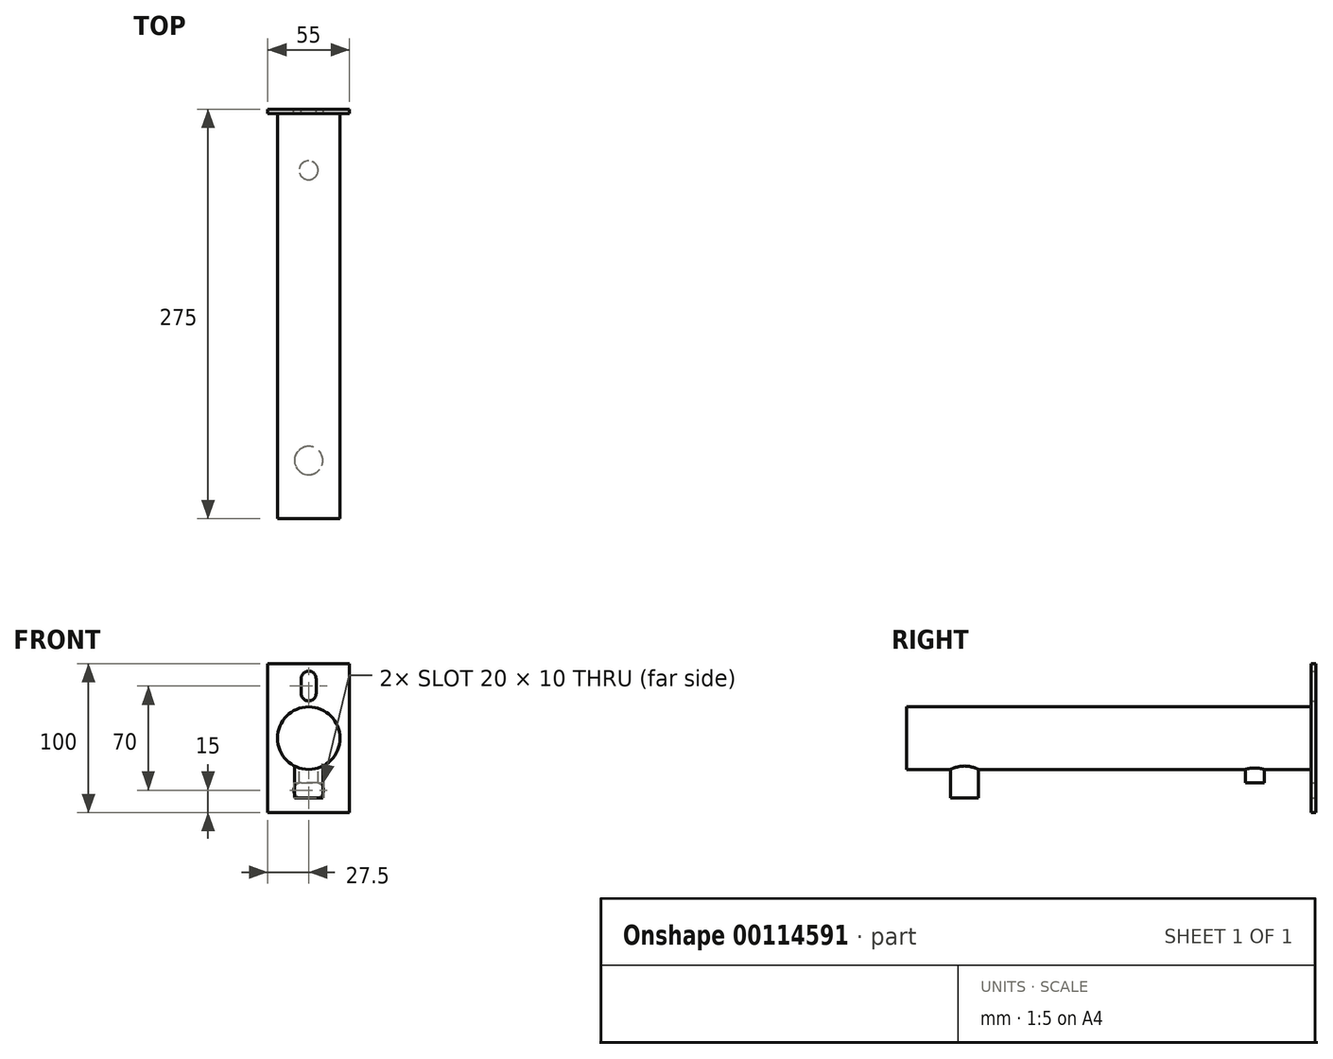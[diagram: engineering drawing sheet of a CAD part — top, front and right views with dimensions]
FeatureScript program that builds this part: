
annotation { "Feature Type Name" : "Feature", "Feature Type Description" : "" }
export const myFeature = defineFeature(function(context is Context, id is Id, definition is map)
    precondition{}
    {
        {
            var Q0;
            Q0=qCreatedBy(makeId("Front.planeOp"),FACE);
            var sketch = newSketch(context, id + "F0", { "sketchPlane" : qUnion([Q0])});
            skLineSegment(sketch, "E0.bottom", {"start": v(-27.5, -50) * mm, "end": v(27.5, -50) * mm});
            skLineSegment(sketch, "E0.top", {"start": v(-27.5, 50) * mm, "end": v(27.5, 50) * mm});
            skLineSegment(sketch, "E0.left", {"start": v(-27.5, -50) * mm, "end": v(-27.5, 50) * mm});
            skLineSegment(sketch, "E0.right", {"start": v(27.5, -50) * mm, "end": v(27.5, 50) * mm});
            skLineSegment(sketch, "E1", {"start": v(-27.5, 0) * mm, "end": v(27.5, 0) * mm, "construction": true});
            skLineSegment(sketch, "E2", {"start": v(0, 50) * mm, "end": v(0, -50) * mm, "construction": true});
            skArc(sketch, "E3", {"start": v(-5, 40) * mm, "mid": v(0, 45) * mm, "end": v(5, 40) * mm});
            skArc(sketch, "E4", {"start": v(-5, 30) * mm, "mid": v(0, 25) * mm, "end": v(5, 30) * mm});
            skLineSegment(sketch, "E5", {"start": v(-5, 40) * mm, "end": v(-5, 30) * mm});
            skLineSegment(sketch, "E6", {"start": v(5, 40) * mm, "end": v(5, 30) * mm});
            skLineSegment(sketch, "E7", {"start": v(-27.5, -35) * mm, "end": v(27.5, -35) * mm, "construction": true});
            skLineSegment(sketch, "E8", {"start": v(-5, -30) * mm, "end": v(0, -30) * mm});
            skArc(sketch, "E9", {"start": v(-5, -30) * mm, "mid": v(-8.54, -31.46) * mm, "end": v(-10, -35) * mm});
            skLineSegment(sketch, "E10.MirrorCS", {"start": v(-5, -40) * mm, "end": v(0, -40) * mm});
            skArc(sketch, "E11.MirrorCS", {"start": v(-5, -40) * mm, "mid": v(-8.54, -38.54) * mm, "end": v(-10, -35) * mm});
            skLineSegment(sketch, "E12.MirrorCS", {"start": v(5, -30) * mm, "end": v(0, -30) * mm});
            skArc(sketch, "E13.MirrorCS", {"start": v(5, -30) * mm, "mid": v(8.54, -31.46) * mm, "end": v(10, -35) * mm});
            skArc(sketch, "E14.MirrorCS", {"start": v(5, -40) * mm, "mid": v(8.54, -38.54) * mm, "end": v(10, -35) * mm});
            skLineSegment(sketch, "E15.MirrorCS", {"start": v(5, -40) * mm, "end": v(0, -40) * mm});
            skSolve(sketch);
        }
        {
            var Q0;
            Q0=makeQuery(id+"F0.imprint","IMPRINT",FACE,{"disambiguationData":[TD([[makeQuery(id+"F0.imprint","IMPRINT",EDGE,{"derivedFrom":sQuery(id+"F0.wireOp",EDGE,"E0.bottom")}),1.0]])]});
            var Q1;
            Q1=makeQuery(id+"F0.imprint","IMPRINT",FACE,{"disambiguationData":[TD([[makeQuery(id+"F0.imprint","IMPRINT",EDGE,{"derivedFrom":sQuery(id+"F0.wireOp",EDGE,"MxBViazi-fYnK-o5l4-c0Sk-fpSHu9DHOUUI")}),1.0]])]});
            extrude(context, id + "F1", {"entities" : qUnion([Q0, Q1]), "depth" : 3 * mm});
        }
        {
            var Q0;
            Q0=makeQuery(id+"F1.opExtrude","CAP_FACE",FACE,{"disambiguationData":[OSD([sQuery(id+"F0.wireOp",EDGE,"E0.bottom"),sQuery(id+"F0.wireOp",EDGE,"E0.top"),sQuery(id+"F0.wireOp",EDGE,"E0.left"),sQuery(id+"F0.wireOp",EDGE,"E0.right"),sQuery(id+"F0.wireOp",EDGE,"E3"),sQuery(id+"F0.wireOp",EDGE,"E4"),sQuery(id+"F0.wireOp",EDGE,"E5"),sQuery(id+"F0.wireOp",EDGE,"E6"),sQuery(id+"F0.wireOp",EDGE,"E8"),sQuery(id+"F0.wireOp",EDGE,"E9"),sQuery(id+"F0.wireOp",EDGE,"E10.MirrorCS"),sQuery(id+"F0.wireOp",EDGE,"E11.MirrorCS"),sQuery(id+"F0.wireOp",EDGE,"E12.MirrorCS"),sQuery(id+"F0.wireOp",EDGE,"E13.MirrorCS"),sQuery(id+"F0.wireOp",EDGE,"E14.MirrorCS"),sQuery(id+"F0.wireOp",EDGE,"E15.MirrorCS")])],"isStart":false});
            var sketch = newSketch(context, id + "F2", { "sketchPlane" : qUnion([Q0])});
            skCircle(sketch, "E16", {"center": v(0, 0) * mm, "radius": 21 * mm});
            skSolve(sketch);
        }
        {
            var Q0;
            Q0=makeQuery(id+"F2.imprint","IMPRINT",FACE,{"disambiguationData":[TD([[makeQuery(id+"F2.imprint","IMPRINT",EDGE,{"derivedFrom":sQuery(id+"F2.wireOp",EDGE,"E16")}),1.0]])]});
            extrude(context, id + "F3", {"entities" : qUnion([Q0]), "operationType" : NewBodyOperationType.ADD, "depth" : (275 - 3) * mm});
        }
        {
            var Q0;
            Q0=qCreatedBy(makeId("Top.planeOp"),FACE);
            var sketch = newSketch(context, id + "F4", { "sketchPlane" : qUnion([Q0])});
            skCircle(sketch, "E17", {"center": v(0, -41) * mm, "radius": 6.35 * mm});
            skCircle(sketch, "E18", {"center": v(0, -236) * mm, "radius": 9.53 * mm});
            skSolve(sketch);
        }
        {
            var Q0;
            Q0=makeQuery(id+"F4.imprint","IMPRINT",FACE,{"disambiguationData":[TD([[makeQuery(id+"F4.imprint","IMPRINT",EDGE,{"derivedFrom":sQuery(id+"F4.wireOp",EDGE,"E17")}),1.0]])]});
            extrude(context, id + "F5", {"entities" : qUnion([Q0]), "operationType" : NewBodyOperationType.ADD, "oppositeDirection" : true, "depth" : 30 * mm});
        }
        {
            var Q0;
            Q0=makeQuery(id+"F4.imprint","IMPRINT",FACE,{"disambiguationData":[TD([[makeQuery(id+"F4.imprint","IMPRINT",EDGE,{"derivedFrom":sQuery(id+"F4.wireOp",EDGE,"E18")}),1.0]])]});
            extrude(context, id + "F6", {"entities" : qUnion([Q0]), "operationType" : NewBodyOperationType.ADD, "oppositeDirection" : true, "depth" : 40 * mm});
        }
    });
